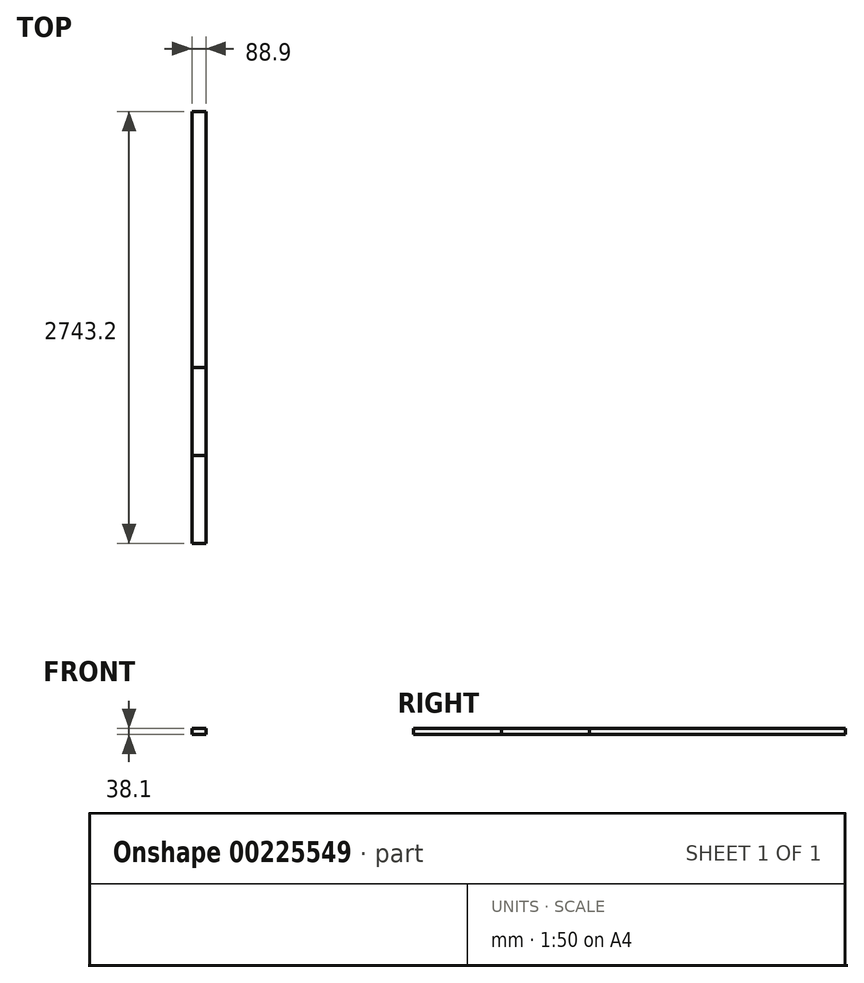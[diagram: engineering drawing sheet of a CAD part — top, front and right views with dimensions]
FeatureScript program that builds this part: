
annotation { "Feature Type Name" : "Feature", "Feature Type Description" : "" }
export const myFeature = defineFeature(function(context is Context, id is Id, definition is map)
    precondition{}
    {
        {
            var Q0;
            Q0=qCreatedBy(makeId("Front.planeOp"),FACE);
            var sketch = newSketch(context, id + "F0", { "sketchPlane" : qUnion([Q0])});
            skLineSegment(sketch, "E0.bottom", {"start": v(-44.45, 19.05) * mm, "end": v(44.45, 19.05) * mm});
            skLineSegment(sketch, "E0.top", {"start": v(-44.45, -19.05) * mm, "end": v(44.45, -19.05) * mm});
            skLineSegment(sketch, "E0.left", {"start": v(-44.45, 19.05) * mm, "end": v(-44.45, -19.05) * mm});
            skLineSegment(sketch, "E0.right", {"start": v(44.45, 19.05) * mm, "end": v(44.45, -19.05) * mm});
            skSolve(sketch);
        }
        {
            var Q0;
            Q0=makeQuery(id+"F0.imprint","IMPRINT",FACE,{"disambiguationData":[TD([[makeQuery(id+"F0.imprint","IMPRINT",EDGE,{"derivedFrom":sQuery(id+"F0.wireOp",EDGE,"E0.bottom")}),-1.0]])]});
            extrude(context, id + "F1", {"entities" : qUnion([Q0]), "oppositeDirection" : true, "depth" : 1625.6 * mm});
        }
        {
            var Q0;
            Q0 = qSketchRegion(id + "F0", true);
            extrude(context, id + "F2", {"entities" : qUnion([Q0]), "depth" : 1117.6 * mm});
        }
        {
            var Q0;
            Q0 = qSketchRegion(id + "F0", true);
            extrude(context, id + "F3", {"entities" : qUnion([Q0]), "depth" : 558.8 * mm});
        }
    });
